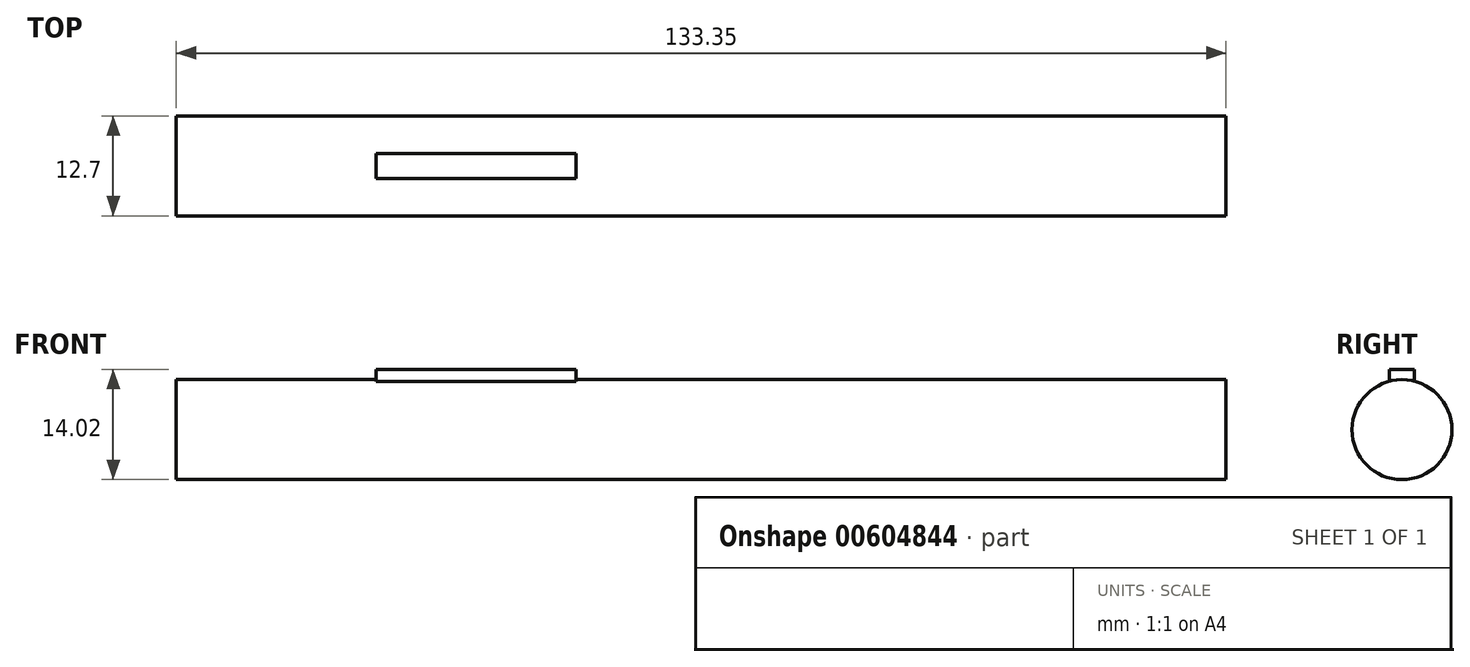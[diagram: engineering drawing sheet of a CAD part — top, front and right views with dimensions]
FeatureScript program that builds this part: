
annotation { "Feature Type Name" : "Feature", "Feature Type Description" : "" }
export const myFeature = defineFeature(function(context is Context, id is Id, definition is map)
    precondition{}
    {
        {
            var Q0;
            Q0=qCreatedBy(makeId("Front.planeOp"),FACE);
            var sketch = newSketch(context, id + "F0", { "sketchPlane" : qUnion([Q0])});
            skLineSegment(sketch, "E0.bottom", {"start": v(-3.96, 0) * mm, "end": v(129.4, 0) * mm});
            skLineSegment(sketch, "E0.top", {"start": v(-3.96, 6.35) * mm, "end": v(129.4, 6.35) * mm});
            skLineSegment(sketch, "E0.left", {"start": v(-3.96, 0) * mm, "end": v(-3.96, 6.35) * mm});
            skLineSegment(sketch, "E0.right", {"start": v(129.4, 0) * mm, "end": v(129.4, 6.35) * mm});
            skSolve(sketch);
        }
        {
            var Q0;
            Q0=makeQuery(id+"F0.imprint","IMPRINT",FACE,{"disambiguationData":[TD([[makeQuery(id+"F0.imprint","IMPRINT",EDGE,{"derivedFrom":sQuery(id+"F0.wireOp",EDGE,"E0.bottom")}),1.0]])]});
            var Q1;
            Q1=sQuery(id+"F0.wireOp",EDGE,"E0.bottom");
            revolve(context, id + "F1", {"entities" : qUnion([Q0]), "axis" : qUnion([Q1]), "revolveType" : RevolveType.FULL});
        }
        {
            var Q0;
            Q0=makeQuery(id+"F1.opRevolve","SWEPT_FACE",FACE,{"disambiguationData":[OSD([sQuery(id+"F0.wireOp",EDGE,"E0.left")])]});
            var sketch = newSketch(context, id + "F2", { "sketchPlane" : qUnion([Q0])});
            skLineSegment(sketch, "E1", {"start": v(-1.59, 6.15) * mm, "end": v(1.59, 6.15) * mm});
            skLineSegment(sketch, "E2", {"start": v(1.59, 6.15) * mm, "end": v(1.59, 7.67) * mm});
            skLineSegment(sketch, "E3", {"start": v(1.59, 7.67) * mm, "end": v(-1.59, 7.67) * mm});
            skLineSegment(sketch, "E4", {"start": v(-1.59, 7.67) * mm, "end": v(-1.59, 6.15) * mm});
            skSolve(sketch);
        }
        {
            var Q0;
            {var subQ0=sQuery(id+"F2.wireOp",EDGE,"E2");Q0=makeQuery(id+"F2.imprint","IMPRINT",FACE,{"disambiguationData":[TD([[makeQuery(id+"F2.imprint","IMPRINT",EDGE,{"derivedFrom":subQ0}),1.0]])]});}
            extrude(context, id + "F3", {"entities" : qUnion([Q0]), "operationType" : NewBodyOperationType.ADD, "oppositeDirection" : true, "depth" : 50.8 * mm, "offsetDistance" : 25 * mm});
        }
        {
            var Q0;
            {var subQ0=sQuery(id+"F0.wireOp",EDGE,"E0.left");Q0=makeQuery(id+"F3.boolean.opBoolean","MERGE",FACE,{"derivedFrom":[makeQuery(id+"F1.opRevolve","SWEPT_FACE",FACE,{"disambiguationData":[OSD([subQ0])]}),makeQuery(id+"F3.opExtrude","CAP_FACE",FACE,{"disambiguationData":[OSD([sQuery(id+"F0.wireOp",EDGE,"E0.top"),subQ0,sQuery(id+"F2.wireOp",EDGE,"E2"),sQuery(id+"F2.wireOp",EDGE,"E3"),sQuery(id+"F2.wireOp",EDGE,"E4")])],"isStart":true})]});}
            var sketch = newSketch(context, id + "F4", { "sketchPlane" : qUnion([Q0])});
            skCircle(sketch, "E5", {"center": v(0, 0) * mm, "radius": 6.35 * mm});
            skLineSegment(sketch, "E6", {"start": v(-1.59, 6.15) * mm, "end": v(-1.59, 7.67) * mm});
            skLineSegment(sketch, "E7", {"start": v(-1.59, 7.67) * mm, "end": v(1.59, 7.67) * mm});
            skLineSegment(sketch, "E8", {"start": v(1.59, 7.67) * mm, "end": v(1.59, 6.15) * mm});
            skSolve(sketch);
        }
        {
            var Q0;
            {var subQ0=sQuery(id+"F4.wireOp",EDGE,"E6");Q0=makeQuery(id+"F4.imprint","IMPRINT",FACE,{"disambiguationData":[TD([[makeQuery(id+"F4.imprint","IMPRINT",EDGE,{"derivedFrom":subQ0}),1.0]])]});}
            extrude(context, id + "F5", {"entities" : qUnion([Q0]), "operationType" : NewBodyOperationType.REMOVE, "oppositeDirection" : true, "depth" : 25.4 * mm, "offsetDistance" : 25 * mm});
        }
    });
